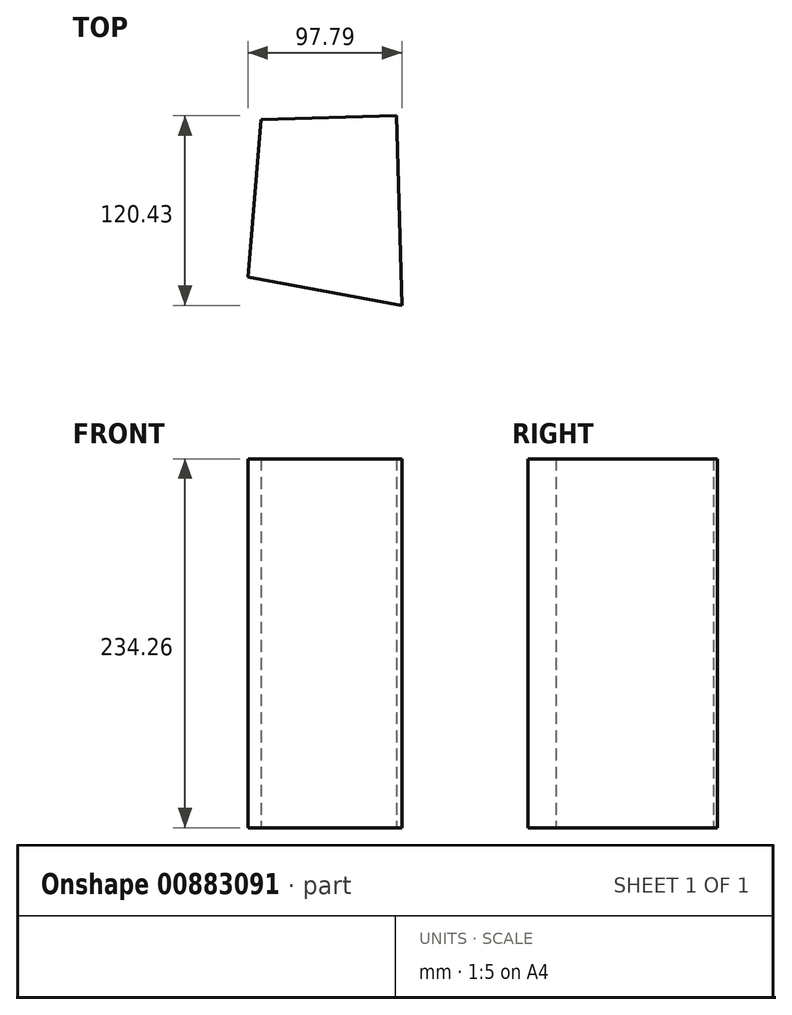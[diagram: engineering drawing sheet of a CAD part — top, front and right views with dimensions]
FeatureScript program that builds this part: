
annotation { "Feature Type Name" : "Feature", "Feature Type Description" : "" }
export const myFeature = defineFeature(function(context is Context, id is Id, definition is map)
    precondition{}
    {
        {
            var Q0;
            Q0=qCreatedBy(makeId("Top.planeOp"),FACE);
            var sketch = newSketch(context, id + "F0", { "sketchPlane" : qUnion([Q0])});
            skLineSegment(sketch, "E0", {"start": v(-37.54, 56.3) * mm, "end": v(48.48, 58.86) * mm});
            skLineSegment(sketch, "E1", {"start": v(48.48, 58.86) * mm, "end": v(52.05, -61.57) * mm});
            skLineSegment(sketch, "E2", {"start": v(52.05, -61.57) * mm, "end": v(-45.74, -43.64) * mm});
            skLineSegment(sketch, "E3", {"start": v(-45.74, -43.64) * mm, "end": v(-37.54, 56.3) * mm});
            skSolve(sketch);
        }
        {
            var Q0;
            Q0=makeQuery(id+"F0.imprint","IMPRINT",FACE,{"disambiguationData":[TD([[makeQuery(id+"F0.imprint","IMPRINT",EDGE,{"derivedFrom":sQuery(id+"F0.wireOp",EDGE,"E0")}),-1.0]])]});
            extrude(context, id + "F1", {"entities" : qUnion([Q0]), "depth" : 117.17 * mm, "offsetDistance" : 25.4 * mm, "hasSecondDirection" : true, "secondDirectionOppositeDirection" : true, "secondDirectionDepth" : 117.1 * mm});
        }
    });
